# Revit family: MECON mag-flux T4 remote coupling
name_source: partatom
category: Rohrzubehör
units: mm (PartAtom-declared; Revit-internal decimal feet)

## family parameters
Arbeitsebenenbasiert = Nein
Beim Laden mit Abzugskörper schneiden = Nein
Bemaßung runder Anschluss = Radius verwenden
Gemeinsam genutzt = Nein
Immer vertikal = Ja
OmniClass-Nummer = 23.60.10.17
OmniClass-Titel = Flow Meters
Teiletyp = Ventil - Zerlegung in

## types (9) — shared parameters
Approval = VdS
Black = Metal - black
Dark Grey = Metal - RAL7024
Delivery Time = app. 3 weeks
Download Test Certificate = https://download.mecon.de
Glass = Glass-
Grey = Metal - grey
Hersteller = MECON GmbH, Röntgenstraße 105, 50169 Kerpen, Germany
IfcExportAs = IfcFlowMeter
IfcExportType = FLOWMETER
Operating Manual = https://www.mecon.de
URL = https://www.mecon.de
VdS Approval = https://www.mecon.de
Website Product = https://www.mecon.de
iFM = Nein
iLPCB = Nein
iVdS = Ja
zero-valued in all types: Vorgabe-Ansicht

## per-type parameters (varying)
| type | Build in Length | Flow Range | Modell | Nominal_Diameter | Nominal_Radius | Order Code | iB | iD1 | iD2 | iH | iR1 |
| DN 200 / 8" 0-18849 l/min, 0-5000 USgpm | 200 mm  [stored 0.656168 ft] | 0 - 10600 l/min. / 0 - 2800 USgpm | Coupling connection 6"/DN 150, lining: hard rubber, electrodes: stainless steel, remote, 230 V AC, 50/60 Hz, 4 - 20 mA, with connector for transducer | 200 mm | 100 mm | T4-H-K150-1-21BB4L | 120 mm  [stored 0.393701 ft] | 285 mm  [stored 0.935039 ft] | 192.5 mm  [stored 0.631562 ft] | 117 mm  [stored 0.383858 ft] | 104 mm |
| DN 300 / 12" 0-42411 l/min, 0-11200 USgpm | 300 mm  [stored 0.984252 ft] | 0 - 42411 l/min. / 0 - 11200 USgpm | Coupling connection 12"/DN 300, lining: hard rubber, electrodes: stainless steel, remote, 230 V AC, 50/60 Hz, 4 - 20 mA, with connector for transducer | 300 mm | 150 mm | T4-H-K300-1-21BB4L | 200 mm  [stored 0.656168 ft] | 520 mm  [stored 1.70604 ft] | 310 mm  [stored 1.01706 ft] | 213 mm  [stored 0.698819 ft] | 154 mm  [stored 0.505249 ft] |
| DN 250 / 10" 0-29452 l/min, 0-7800 USgpm | 300 mm  [stored 0.984252 ft] | 0 - 29500 l/min. / 0 - 7800 USgpm | Coupling connection 10"/DN 250, lining: hard rubber, electrodes: stainless steel, remote, 230 V AC, 50/60 Hz, 4 - 20 mA, with connector for transducer | 250 mm | 125 mm | T4-H-K250-1-21BB4L | 200 mm  [stored 0.656168 ft] | 440 mm  [stored 1.44357 ft] | 270 mm  [stored 0.885827 ft] | 180 mm  [stored 0.590551 ft] | 129 mm  [stored 0.423228 ft] |
| DN 150 / 6" 0-10602 l/min, 0-2800 USgpm | 200 mm  [stored 0.656168 ft] | 0 - 10600 l/min. / 0 - 2800 USgpm | Coupling connection 6"/DN 150, lining: hard rubber, electrodes: stainless steel, remote, 230 V AC, 50/60 Hz, 4 - 20 mA, with connector for transducer | 150 mm | 75 mm | T4-H-K150-1-21BB4L | 120 mm  [stored 0.393701 ft] | 285 mm  [stored 0.935039 ft] | 192.5 mm  [stored 0.631562 ft] | 117 mm  [stored 0.383858 ft] | 79 mm |
| DN 125 / 5", 0-7363 l/min, 0-1950 USgpm | 200 mm  [stored 0.656168 ft] | 0 - 7350 l/min. / 0 - 1950 USgpm | Coupling connection 5"/DN 125, lining: hard rubber, electrodes: stainless steel, remote, 230 V AC, 50/60 Hz, 4 - 20 mA, with connector for transducer | 125 mm | 63 mm | T4-H-K125-1-21BB4L | 120 mm  [stored 0.393701 ft] | 240 mm  [stored 0.787402 ft] | 170 mm  [stored 0.557743 ft] | 98 mm  [stored 0.321522 ft] | 66.5 mm |
| DN 100 / 4", 0-4712 l/min, 0-1250 USgpm | 200 mm  [stored 0.656168 ft] | 0 - 4700 l/min. / 0 - 1250 USgpm | Coupling connection 4"/DN 100, lining: hard rubber, electrodes: stainless steel, remote, 230 V AC, 50/60 Hz, 4 - 20 mA, with connector for transducer | 100 mm | 50 mm | T4-H-K100-1-21BB4L | 120 mm  [stored 0.393701 ft] | 210 mm  [stored 0.688976 ft] | 155 mm  [stored 0.50853 ft] | 86 mm  [stored 0.282152 ft] | 54 mm |
| DN 80 / 3", 0-3015 l/min, 0-800 USgpm | 150 mm  [stored 0.492126 ft] | 0 - 3000 l/min. / 0 - 800 USgpm | Coupling connection 3"/DN 80, lining: hard rubber, electrodes: stainless steel, remote, 230 V AC, 50/60 Hz, 4 - 20 mA, with connector for transducer | 80 mm | 40 mm | T4-H-K080-1-21BB4L | 80 mm  [stored 0.262467 ft] | 170 mm  [stored 0.557743 ft] | 135 mm  [stored 0.442913 ft] | 70 mm  [stored 0.229659 ft] | 44 mm  [stored 0.144357 ft] |
| DN 65 / 2½", 0-1990 l/min, 0-525 USgpm | 150 mm  [stored 0.492126 ft] | 0 - 2000 l/min. / 0 - 525 USgpm | Coupling connection 2 ½"/DN 65, lining: hard rubber, electrodes: stainless steel, remote, 230 V AC, 50/60 Hz, 4 - 20 mA, with connector for transducer | 65 mm | 33 mm | T4-H-K065-1-21BB4L | 80 mm  [stored 0.262467 ft] | 155 mm  [stored 0.50853 ft] | 127.5 mm  [stored 0.418307 ft] | 63 mm  [stored 0.206693 ft] | 36.5 mm  [stored 0.119751 ft] |
| DN 50 / 2", 0-1178 l/min, 0-310 USgpm | 150 mm  [stored 0.492126 ft] | 0 - 1180 l/min / 0 - 310 USgpm | Coupling connection 2"/DN 50, lining: hard rubber, electrodes: stainless steel, remote, 230 V AC, 50/60 Hz, 4 - 20 mA, with connector for transducer | 50 mm | 25 mm | T4-H-K050-1-21BB4L | 80 mm  [stored 0.262467 ft] | 140 mm  [stored 0.459318 ft] | 120 mm  [stored 0.393701 ft] | 57 mm  [stored 0.187008 ft] | 29 mm  [stored 0.0951444 ft] |

note: column(s) folded — value = type name in every type: Typenkommentare

note: [stored X ft] marks values corroborated as IEEE doubles in the binary element streams (Revit-internal decimal feet)
